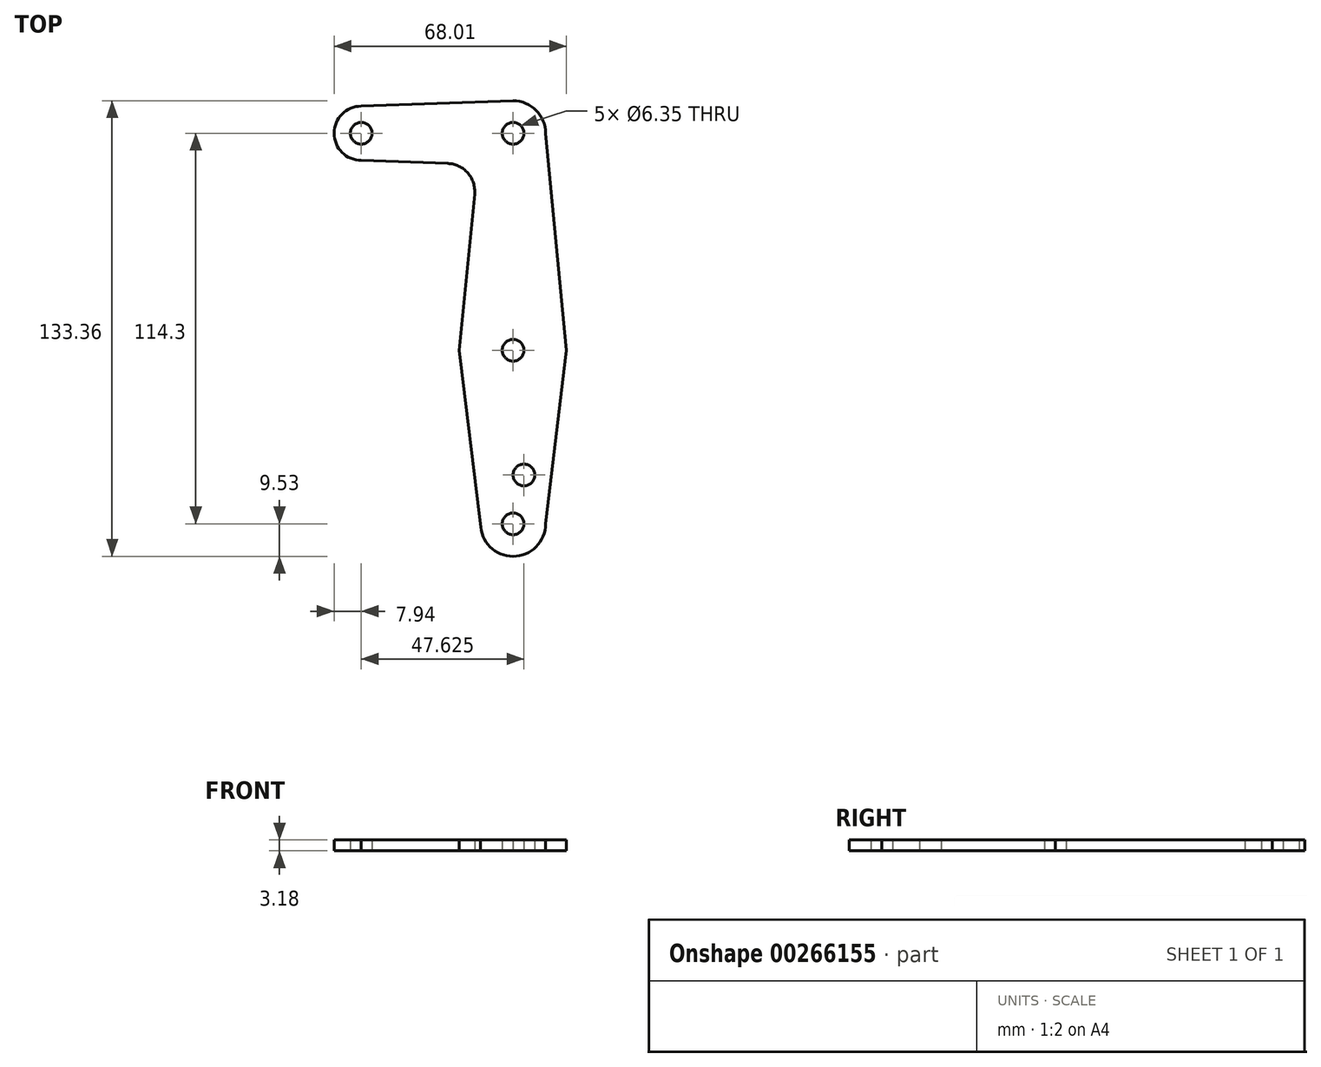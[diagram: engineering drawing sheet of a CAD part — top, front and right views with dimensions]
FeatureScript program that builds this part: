
annotation { "Feature Type Name" : "Feature", "Feature Type Description" : "" }
export const myFeature = defineFeature(function(context is Context, id is Id, definition is map)
    precondition{}
    {
        {
            var Q0;
            Q0=qCreatedBy(makeId("Top.planeOp"),FACE);
            var sketch = newSketch(context, id + "F0", { "sketchPlane" : qUnion([Q0])});
            skCircle(sketch, "E0", {"center": v(0, 0) * mm, "radius": 3.18 * mm});
            skCircle(sketch, "E1", {"center": v(44.45, 0) * mm, "radius": 3.18 * mm});
            skCircle(sketch, "E2", {"center": v(44.45, -63.5) * mm, "radius": 3.18 * mm});
            skCircle(sketch, "E3", {"center": v(44.45, -114.3) * mm, "radius": 3.17 * mm});
            skArc(sketch, "E4", {"start": v(0, 7.94) * mm, "mid": v(-7.94, 0) * mm, "end": v(0, -7.94) * mm});
            skArc(sketch, "E5", {"start": v(53.98, 0) * mm, "mid": v(50.94, 6.97) * mm, "end": v(43.77, 9.5) * mm});
            skArc(sketch, "E6", {"start": v(34.93, -114.3) * mm, "mid": v(44.45, -123.83) * mm, "end": v(53.98, -114.3) * mm});
            skLineSegment(sketch, "E7", {"start": v(34.93, -114.3) * mm, "end": v(28.71, -63.5) * mm});
            skLineSegment(sketch, "E8", {"start": v(28.71, -63.5) * mm, "end": v(33.18, -17.83) * mm});
            skLineSegment(sketch, "E9", {"start": v(0, -7.94) * mm, "end": v(25.32, -8.84) * mm});
            skLineSegment(sketch, "E10", {"start": v(0, 7.94) * mm, "end": v(44.45, 9.52) * mm});
            skLineSegment(sketch, "E11", {"start": v(53.98, 0) * mm, "end": v(60.07, -63.5) * mm});
            skLineSegment(sketch, "E12", {"start": v(60.07, -63.5) * mm, "end": v(53.98, -114.3) * mm});
            skPoint(sketch, "E13.newPointA", {"position": v(44.45, -9.52) * mm});
            skPoint(sketch, "E13.newPointB", {"position": v(34.93, 0) * mm});
            skArc(sketch, "E13.filletArc", {"start": v(33.18, -17.83) * mm, "mid": v(31.2, -11.63) * mm, "end": v(25.32, -8.84) * mm});
            skCircle(sketch, "E14", {"center": v(47.63, -100.01) * mm, "radius": 3.18 * mm});
            skSolve(sketch);
        }
        {
            var Q0;
            Q0=makeQuery(id+"F0.imprint","IMPRINT",FACE,{"disambiguationData":[TD([[makeQuery(id+"F0.imprint","IMPRINT",EDGE,{"derivedFrom":sQuery(id+"F0.wireOp",EDGE,"E0")}),-1.0]])]});
            extrude(context, id + "F1", {"entities" : qUnion([Q0]), "depth" : 3.17 * mm});
        }
    });
